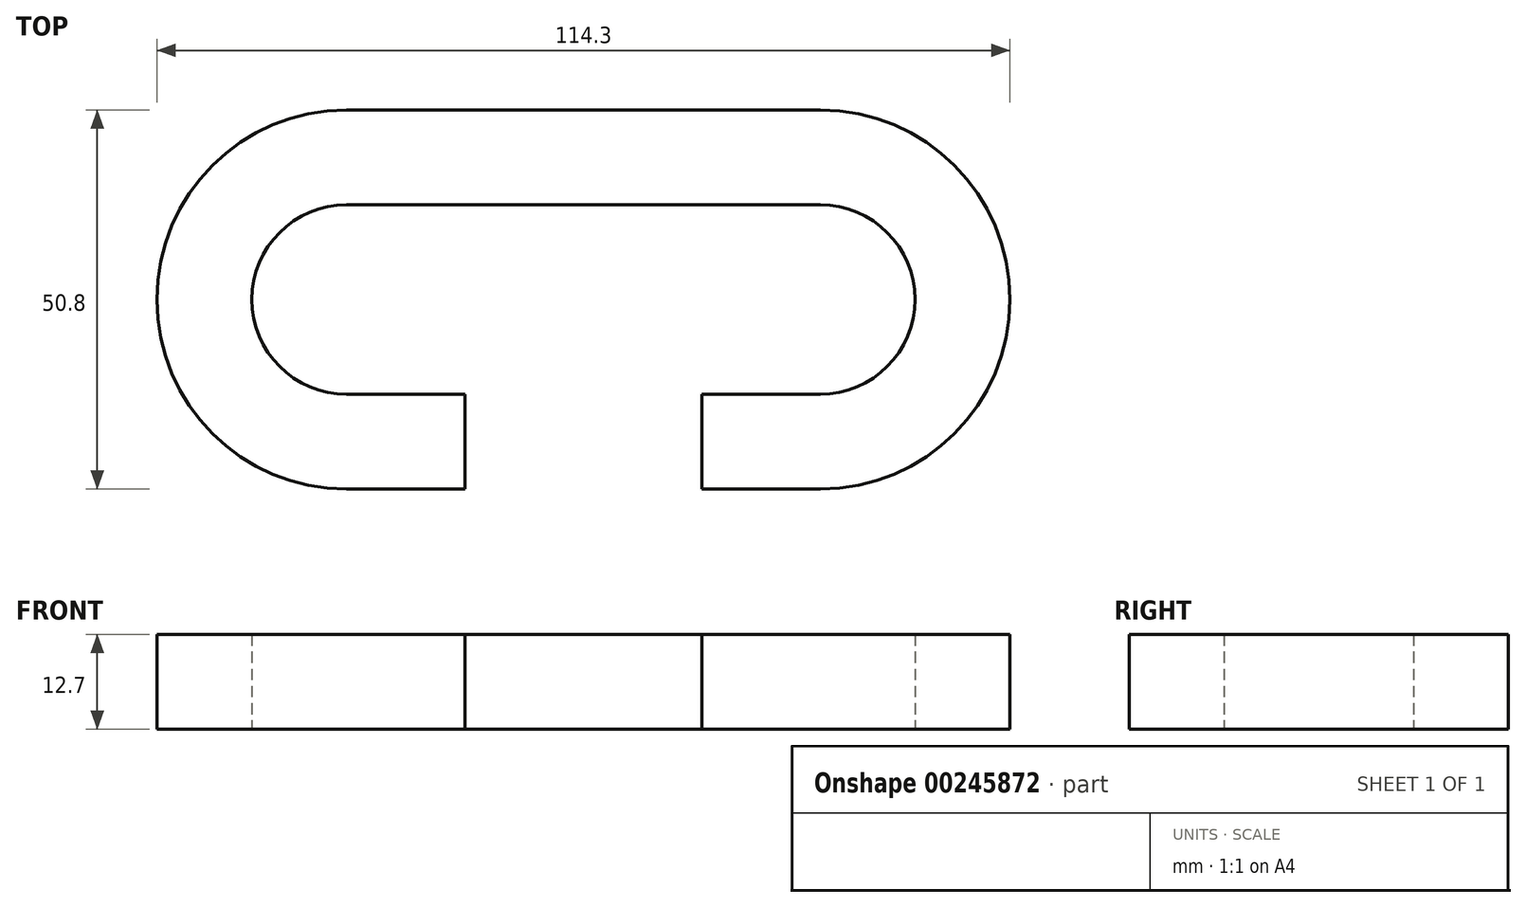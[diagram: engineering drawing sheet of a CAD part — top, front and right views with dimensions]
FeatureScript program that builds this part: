
annotation { "Feature Type Name" : "Feature", "Feature Type Description" : "" }
export const myFeature = defineFeature(function(context is Context, id is Id, definition is map)
    precondition{}
    {
        {
            var Q0;
            Q0=qCreatedBy(makeId("Top.planeOp"),FACE);
            var sketch = newSketch(context, id + "F0", { "sketchPlane" : qUnion([Q0])});
            skArc(sketch, "E0", {"start": v(31.75, -12.7) * mm, "mid": v(44.45, 0) * mm, "end": v(31.75, 12.7) * mm});
            skArc(sketch, "E1", {"start": v(31.75, -25.4) * mm, "mid": v(57.15, 0) * mm, "end": v(31.75, 25.4) * mm});
            skLineSegment(sketch, "E2", {"start": v(31.75, 12.7) * mm, "end": v(0, 12.7) * mm});
            skLineSegment(sketch, "E3", {"start": v(31.75, -25.4) * mm, "end": v(15.88, -25.4) * mm});
            skLineSegment(sketch, "E4", {"start": v(31.75, 25.4) * mm, "end": v(0, 25.4) * mm});
            skLineSegment(sketch, "E5", {"start": v(31.75, -12.7) * mm, "end": v(15.88, -12.7) * mm});
            skLineSegment(sketch, "E6", {"start": v(15.88, -12.7) * mm, "end": v(15.88, -25.4) * mm});
            skPoint(sketch, "E7.orphan", {"position": v(0, -12.7) * mm});
            skPoint(sketch, "E8.orphan", {"position": v(0, -25.4) * mm});
            skLineSegment(sketch, "E9.MirrorCS", {"start": v(-31.75, 25.4) * mm, "end": v(0, 25.4) * mm});
            skLineSegment(sketch, "E10.MirrorCS", {"start": v(-31.75, 12.7) * mm, "end": v(0, 12.7) * mm});
            skArc(sketch, "E11.MirrorCS", {"start": v(-31.75, -25.4) * mm, "mid": v(-57.15, 0) * mm, "end": v(-31.75, 25.4) * mm});
            skArc(sketch, "E12.MirrorCS", {"start": v(-31.75, -12.7) * mm, "mid": v(-44.45, 0) * mm, "end": v(-31.75, 12.7) * mm});
            skLineSegment(sketch, "E13.MirrorCS", {"start": v(-31.75, -12.7) * mm, "end": v(-15.88, -12.7) * mm});
            skLineSegment(sketch, "E14.MirrorCS", {"start": v(-31.75, -25.4) * mm, "end": v(-15.88, -25.4) * mm});
            skLineSegment(sketch, "E15.MirrorCS", {"start": v(-15.88, -12.7) * mm, "end": v(-15.88, -25.4) * mm});
            skSolve(sketch);
        }
        {
            var Q0;
            Q0=makeQuery(id+"F0.imprint","IMPRINT",FACE,{"disambiguationData":[TD([[makeQuery(id+"F0.imprint","IMPRINT",EDGE,{"derivedFrom":sQuery(id+"F0.wireOp",EDGE,"E0")}),-1.0]])]});
            extrude(context, id + "F1", {"entities" : qUnion([Q0]), "depth" : 12.7 * mm});
        }
    });
